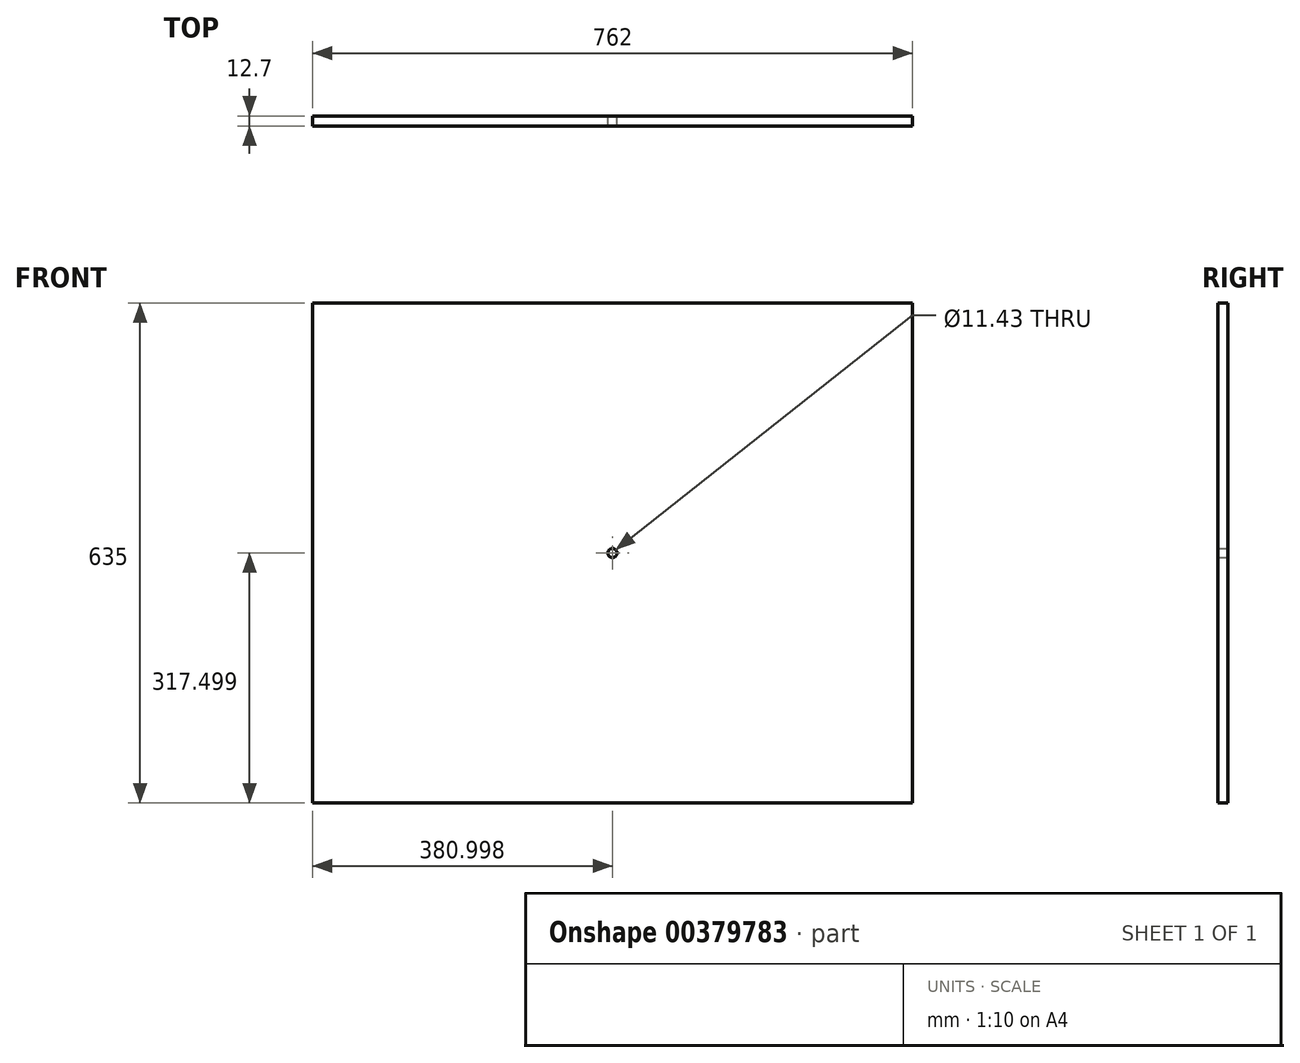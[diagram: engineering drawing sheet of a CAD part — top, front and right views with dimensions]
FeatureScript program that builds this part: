
annotation { "Feature Type Name" : "Feature", "Feature Type Description" : "" }
export const myFeature = defineFeature(function(context is Context, id is Id, definition is map)
    precondition{}
    {
        {
            var Q0;
            Q0=qCreatedBy(makeId("Front.planeOp"),FACE);
            var sketch = newSketch(context, id + "F0", { "sketchPlane" : qUnion([Q0])});
            skLineSegment(sketch, "E0.bottom", {"start": v(-75.3, 558.6) * mm, "end": v(686.7, 558.6) * mm});
            skLineSegment(sketch, "E0.top", {"start": v(-75.3, -76.4) * mm, "end": v(686.7, -76.4) * mm});
            skLineSegment(sketch, "E0.left", {"start": v(-75.3, 558.6) * mm, "end": v(-75.3, -76.4) * mm});
            skLineSegment(sketch, "E0.right", {"start": v(686.7, 558.6) * mm, "end": v(686.7, -76.4) * mm});
            skLineSegment(sketch, "E1", {"start": v(305.7, 558.6) * mm, "end": v(305.7, -76.4) * mm, "construction": true});
            skLineSegment(sketch, "E2", {"start": v(-75.3, 241.1) * mm, "end": v(686.7, 241.1) * mm, "construction": true});
            skCircle(sketch, "E3", {"center": v(305.7, 241.1) * mm, "radius": 5.72 * mm});
            skSolve(sketch);
        }
        {
            var Q0;
            Q0=qSketchRegion(id+"F0",true);
            extrude(context, id + "F1", {"entities" : qUnion([Q0]), "depth" : 12.7 * mm});
        }
    });
